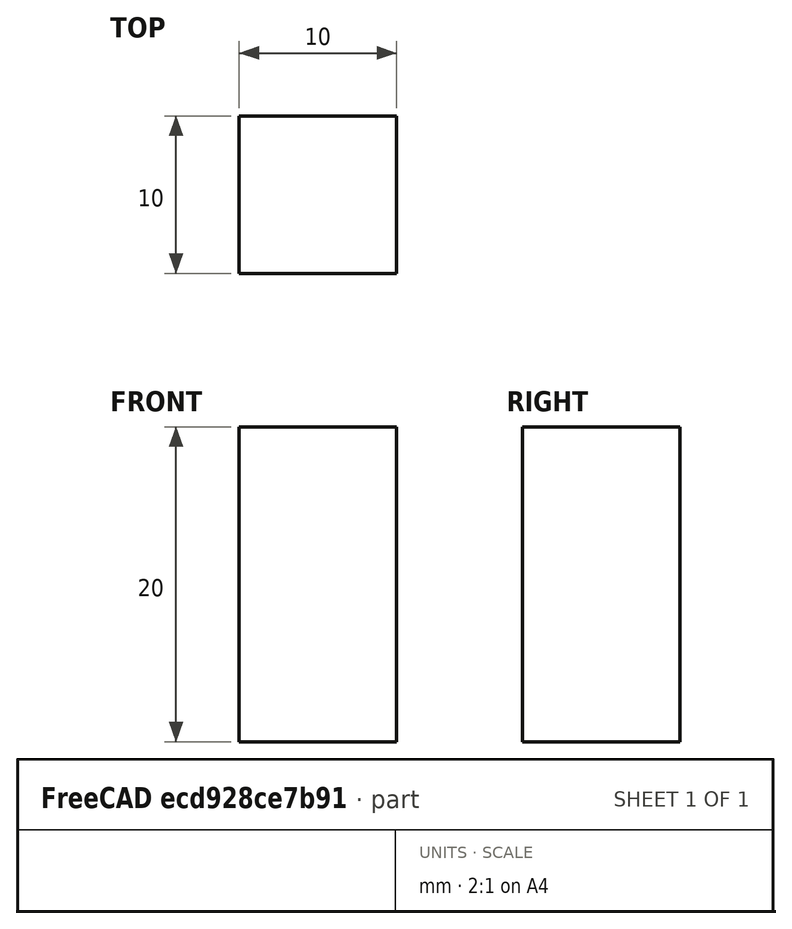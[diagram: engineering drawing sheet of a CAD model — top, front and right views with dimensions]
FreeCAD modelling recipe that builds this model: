
FCSTD DOCUMENT  (FreeCAD 1.1R44874 (Git))
Label: scint-10x10x20mm
License: All rights reserved
LicenseURL: https://en.wikipedia.org/wiki/All_rights_reserved
objects: App::Point×1, Sketcher::SketchObject×1, PartDesign::Pad×1, PartDesign::Body×1, Mesh::Feature×1
note: 6 computed .brp shape members not serialized (recipe doc carries the construction recipe); baked Part::Feature solids carry a one-line shape summary decoded from their .brp

FEATURE [App::Point] Origin001
  Role = Origin
FEATURE [Sketcher::SketchObject] Sketch
  ArcFitTolerance = 1e-06
  AttachmentSupport = -> [Origin]
  ExternalTypes = [0]
  FullyConstrained = true
  MakeInternals = false
  MapMode = 5
  _ExternalGeoVersion = 1
  sketch-geometry (5):
    g0: LineSegment StartX=-5 StartY=-5 StartZ=0 EndX=5 EndY=-5 EndZ=0
    g1: LineSegment StartX=5 StartY=-5 StartZ=0 EndX=5 EndY=5 EndZ=0
    g2: LineSegment StartX=5 StartY=5 StartZ=0 EndX=-5 EndY=5 EndZ=0
    g3: LineSegment StartX=-5 StartY=5 StartZ=0 EndX=-5 EndY=-5 EndZ=0
    g4: GeomPoint [constr] X=0 Y=0 Z=0
  constraints (12):
    c: Coincident(g0,g1)
    c: Coincident(g1,g2)
    c: Coincident(g2,g3)
    c: Coincident(g3,g0)
    c: Horizontal(g0)
    c: Horizontal(g2)
    c: Vertical(g1)
    c: Vertical(g3)
    c: Symmetric(g2,g0,g4)
    c: Distance(g1,g3) = 10
    c: Distance(g0,g2) = 10
    c: Coincident(g4,g-1)
FEATURE [PartDesign::Pad] Pad
  Direction = (0,0,1)
  Length = 20
  Length2 = 10
  Profile = -> Sketch
  ReferenceAxis = -> Sketch [N_Axis]
  Refine = true
  SideType = 0
  Suppressed = false
  Type = 0
  Type2 = 0
FEATURE [PartDesign::Body] Body
  AllowCompound = true
  Group = -> [Sketch,Pad]
  Origin = -> Origin
  Tip = -> Pad
FEATURE [Mesh::Feature] Mesh  label="Body (Meshed)"
